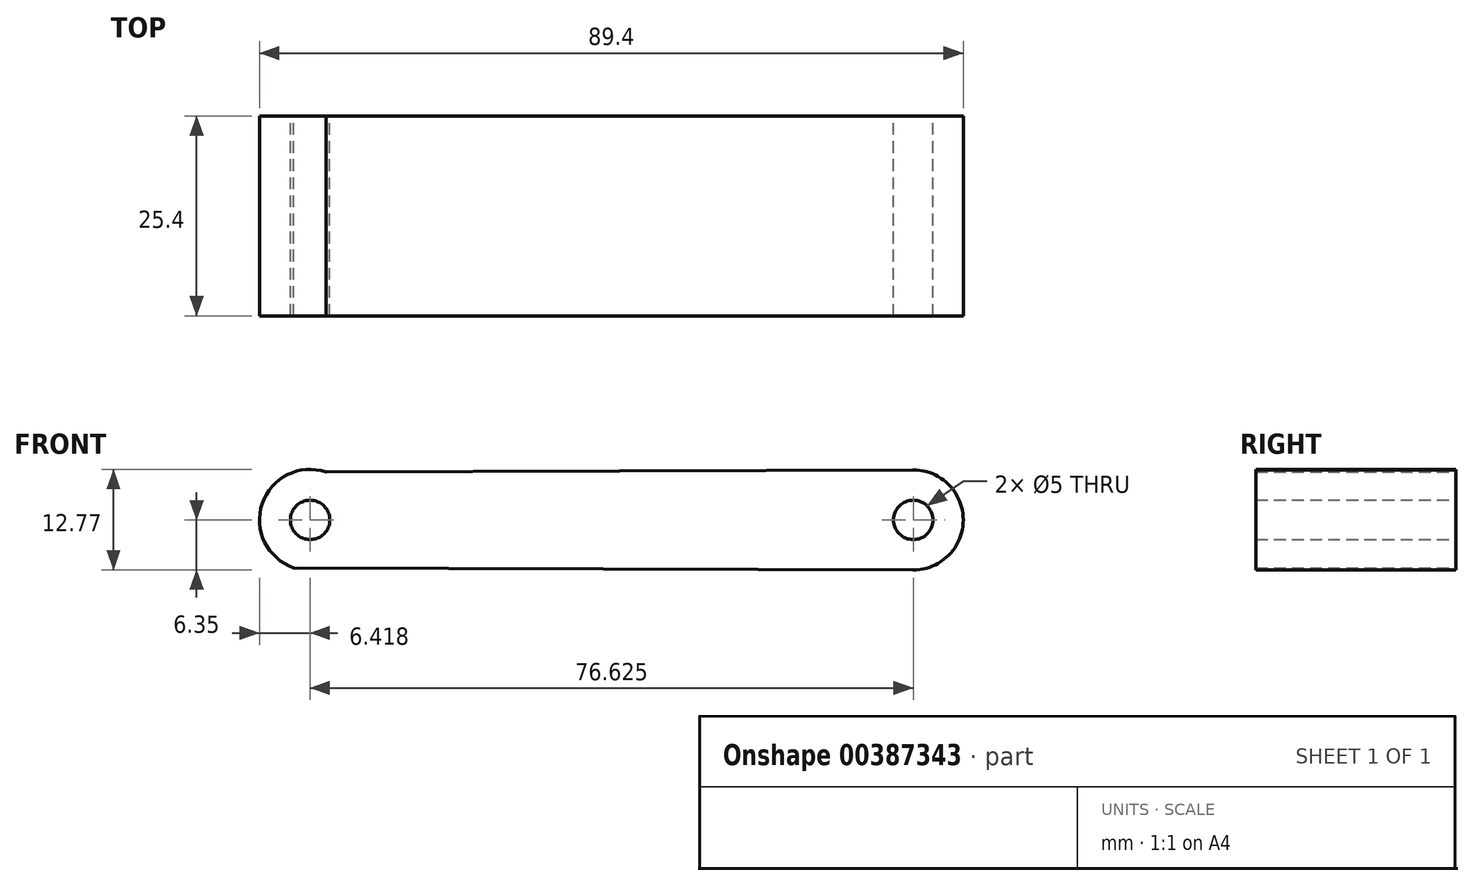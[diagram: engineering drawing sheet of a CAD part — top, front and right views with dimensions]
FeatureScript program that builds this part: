
annotation { "Feature Type Name" : "Feature", "Feature Type Description" : "" }
export const myFeature = defineFeature(function(context is Context, id is Id, definition is map)
    precondition{}
    {
        {
            var Q0;
            Q0=qCreatedBy(makeId("Front.planeOp"),FACE);
            var sketch = newSketch(context, id + "F0", { "sketchPlane" : qUnion([Q0])});
            skCircle(sketch, "E0", {"center": v(-36.06, 0) * mm, "radius": 2.5 * mm});
            skCircle(sketch, "E1", {"center": v(40.56, 0) * mm, "radius": 2.5 * mm});
            skArc(sketch, "E2", {"start": v(-34.03, 6.09) * mm, "mid": v(-42.14, 2.05) * mm, "end": v(-38.14, -6.07) * mm});
            skArc(sketch, "E3", {"start": v(40.54, -6.35) * mm, "mid": v(46.92, 0) * mm, "end": v(40.54, 6.35) * mm});
            skLineSegment(sketch, "E4", {"start": v(-38.14, -6.07) * mm, "end": v(42.08, -6.36) * mm});
            skLineSegment(sketch, "E5", {"start": v(-38.14, 6.07) * mm, "end": v(42.08, 6.36) * mm});
            skSolve(sketch);
        }
        {
            var Q0;
            Q0 = qSketchRegion(id + "F0", true);
            extrude(context, id + "F1", {"entities" : qUnion([Q0]), "depth" : 25.4 * mm});
        }
    });
